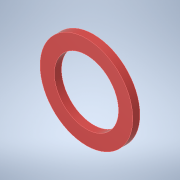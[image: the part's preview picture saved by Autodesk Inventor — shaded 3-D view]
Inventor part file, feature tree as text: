
AUTODESK INVENTOR PART (.ipt)
format: ipt  version: 2022.3 (Build 263350000, 350)  size: 108,544 bytes
history: native  units: in
note: dims shown in document units (in); Inventor stores cm internally (conversion verified against a paired STEP export)
features: sketch x1, extrude x1
ambient origin geometry x8: Origin, YZ Plane, XZ Plane, XY Plane, X Axis, Y Axis, Z Axis, Center Point
bodies: Solid1 (feature_tree)
feature tree (2):
  sketch  "Sketch1"  dims[d1=0.0625in d2=0.0in d13=0.561in d14=0.125in]
  extrude  "Extrusion1"  TaperAngle=0.0deg  [1 undecoded]
note: 1 required parameter value undecoded (feature->parameter linkage not recoverable at this tier; creation-order binding heuristic only, values carry confidence <= 0.55)
